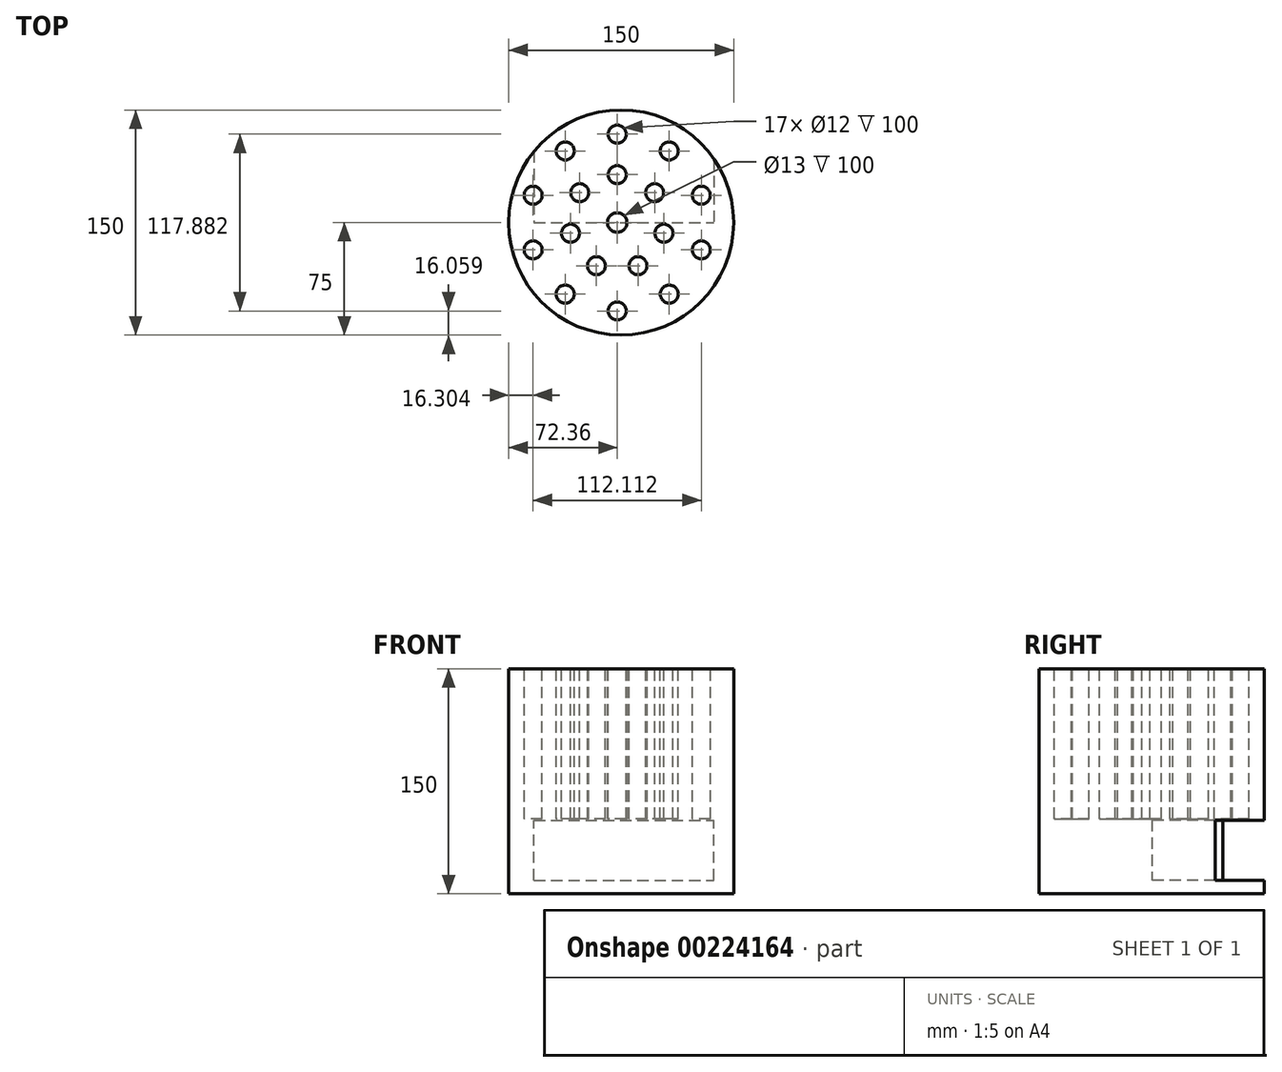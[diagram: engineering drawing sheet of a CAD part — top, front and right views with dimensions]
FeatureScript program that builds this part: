
annotation { "Feature Type Name" : "Feature", "Feature Type Description" : "" }
export const myFeature = defineFeature(function(context is Context, id is Id, definition is map)
    precondition{}
    {
        {
            var Q0;
            Q0=qCreatedBy(makeId("Top.planeOp"),FACE);
            var sketch = newSketch(context, id + "F0", { "sketchPlane" : qUnion([Q0])});
            skCircle(sketch, "E0", {"center": v(2.64, 0) * mm, "radius": 75 * mm});
            skSolve(sketch);
        }
        {
            var Q0;
            Q0=makeQuery(id+"F0.imprint","IMPRINT",FACE,{"disambiguationData":[TD([[makeQuery(id+"F0.imprint","IMPRINT",EDGE,{"derivedFrom":sQuery(id+"F0.wireOp",EDGE,"E0")}),1.0]])]});
            var sketch = newSketch(context, id + "F1", { "sketchPlane" : qUnion([Q0])});
            skCircle(sketch, "E1", {"center": v(0, 58.94) * mm, "radius": 6 * mm});
            skCircle(sketch, "E2.1.0", {"center": v(-34.64, 47.68) * mm, "radius": 6 * mm});
            skCircle(sketch, "E2.2.0", {"center": v(-56.06, 18.21) * mm, "radius": 6 * mm});
            skCircle(sketch, "E2.3.0", {"center": v(-56.06, -18.21) * mm, "radius": 6 * mm});
            skCircle(sketch, "E2.4.0", {"center": v(-34.64, -47.68) * mm, "radius": 6 * mm});
            skCircle(sketch, "E2.5.0", {"center": v(0, -58.94) * mm, "radius": 6 * mm});
            skCircle(sketch, "E2.6.0", {"center": v(34.64, -47.68) * mm, "radius": 6 * mm});
            skCircle(sketch, "E2.7.0", {"center": v(56.06, -18.21) * mm, "radius": 6 * mm});
            skCircle(sketch, "E2.8.0", {"center": v(56.06, 18.21) * mm, "radius": 6 * mm});
            skCircle(sketch, "E2.9.0", {"center": v(34.64, 47.68) * mm, "radius": 6 * mm});
            skPoint(sketch, "E2.center", {"position": v(0, 0) * mm});
            skCircle(sketch, "E3", {"center": v(0, 31.94) * mm, "radius": 6 * mm});
            skCircle(sketch, "E4.1.0", {"center": v(-24.97, 19.91) * mm, "radius": 6 * mm});
            skCircle(sketch, "E4.2.0", {"center": v(-31.14, -7.1) * mm, "radius": 6 * mm});
            skCircle(sketch, "E4.3.0", {"center": v(-13.86, -28.78) * mm, "radius": 6 * mm});
            skCircle(sketch, "E4.4.0", {"center": v(13.86, -28.78) * mm, "radius": 6 * mm});
            skCircle(sketch, "E4.5.0", {"center": v(31.14, -7.1) * mm, "radius": 6 * mm});
            skCircle(sketch, "E4.6.0", {"center": v(24.97, 19.91) * mm, "radius": 6 * mm});
            skCircle(sketch, "E5", {"center": v(0, 0) * mm, "radius": 6.5 * mm});
            skSolve(sketch);
        }
        {
            var Q0;
            Q0=makeQuery(id+"F0.imprint","IMPRINT",FACE,{"disambiguationData":[TD([[makeQuery(id+"F0.imprint","IMPRINT",EDGE,{"derivedFrom":sQuery(id+"F0.wireOp",EDGE,"E0")}),1.0]])]});
            extrude(context, id + "F2", {"entities" : qUnion([Q0]), "oppositeDirection" : true, "depth" : 150 * mm});
        }
        {
            var Q0;
            Q0 = qSketchRegion(id + "F1", true);
            extrude(context, id + "F3", {"entities" : qUnion([Q0]), "operationType" : NewBodyOperationType.REMOVE, "oppositeDirection" : true, "depth" : 100 * mm});
        }
        {
            var Q0;
            Q0=qCreatedBy(makeId("Front.planeOp"),FACE);
            var sketch = newSketch(context, id + "F4", { "sketchPlane" : qUnion([Q0])});
            skLineSegment(sketch, "E6.bottom", {"start": v(-55.53, -100.89) * mm, "end": v(64.47, -100.89) * mm});
            skLineSegment(sketch, "E6.top", {"start": v(-55.53, -140.89) * mm, "end": v(64.47, -140.89) * mm});
            skLineSegment(sketch, "E6.left", {"start": v(-55.53, -100.89) * mm, "end": v(-55.53, -140.89) * mm});
            skLineSegment(sketch, "E6.right", {"start": v(64.47, -100.89) * mm, "end": v(64.47, -140.89) * mm});
            skSolve(sketch);
        }
        {
            var Q0;
            Q0 = qSketchRegion(id + "F4", true);
            extrude(context, id + "F5", {"entities" : qUnion([Q0]), "operationType" : NewBodyOperationType.REMOVE, "oppositeDirection" : true, "depth" : 90 * mm});
        }
    });
